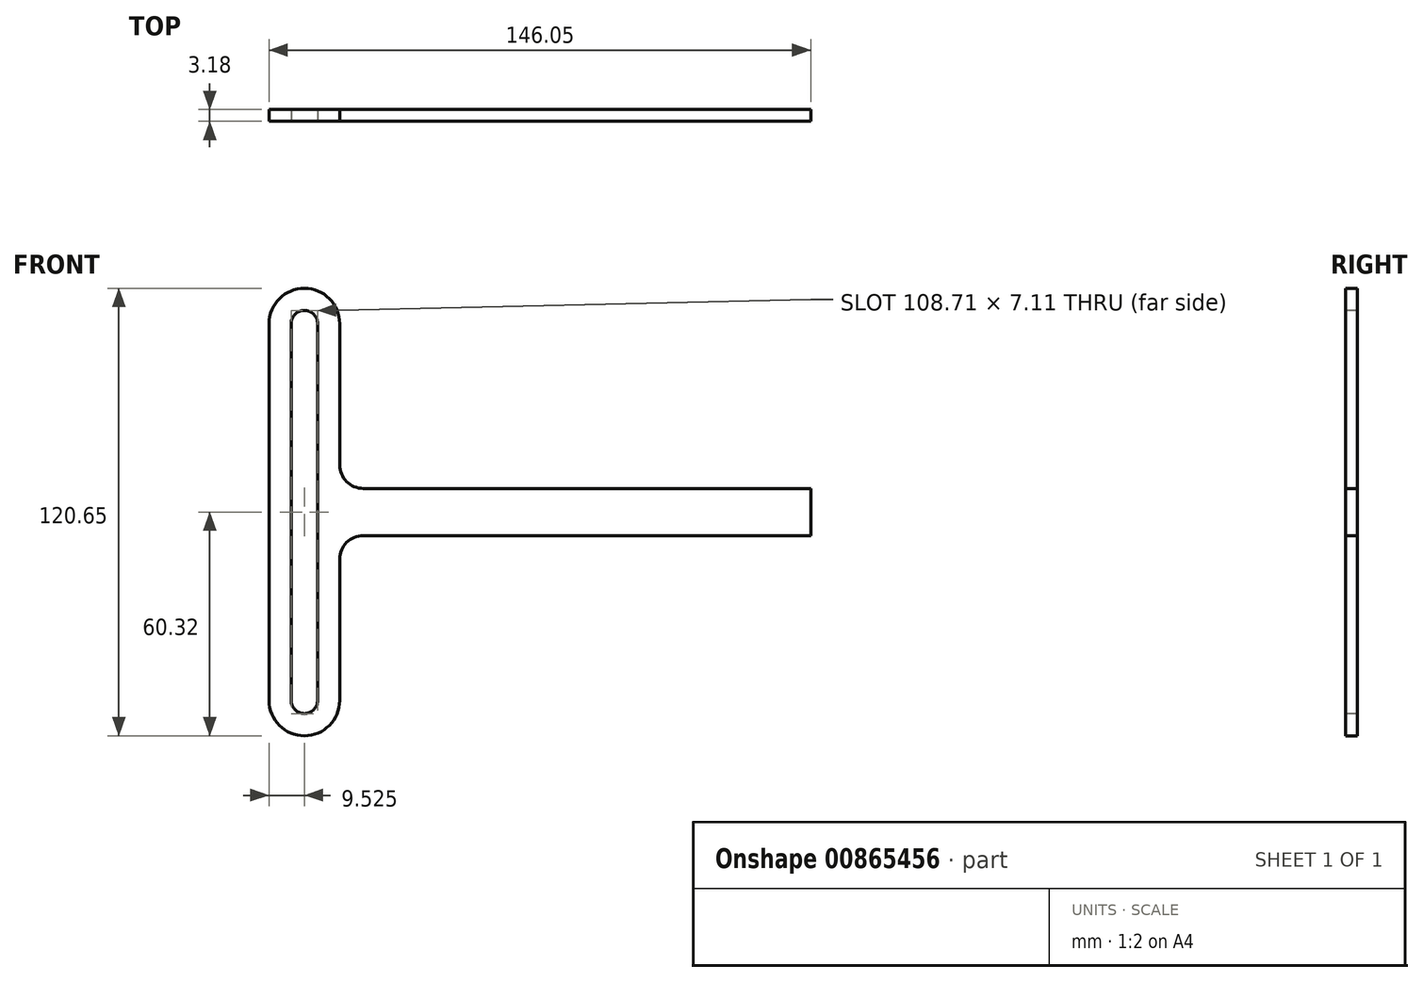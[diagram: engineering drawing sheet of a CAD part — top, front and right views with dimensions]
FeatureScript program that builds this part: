
annotation { "Feature Type Name" : "Feature", "Feature Type Description" : "" }
export const myFeature = defineFeature(function(context is Context, id is Id, definition is map)
    precondition{}
    {
        {
            var Q0;
            Q0=qCreatedBy(makeId("Front.planeOp"),FACE);
            var sketch = newSketch(context, id + "F0", { "sketchPlane" : qUnion([Q0])});
            skLineSegment(sketch, "E0.bottom", {"start": v(6.35, 0) * mm, "end": v(127, 0) * mm});
            skLineSegment(sketch, "E0.top", {"start": v(6.35, -12.7) * mm, "end": v(127, -12.7) * mm});
            skLineSegment(sketch, "E0.right", {"start": v(127, 0) * mm, "end": v(127, -12.7) * mm});
            skLineSegment(sketch, "E1", {"start": v(0, 6.35) * mm, "end": v(0, 44.45) * mm});
            skLineSegment(sketch, "E2", {"start": v(-19.05, 44.45) * mm, "end": v(-19.05, -57.15) * mm});
            skLineSegment(sketch, "E3", {"start": v(0, -57.15) * mm, "end": v(0, -19.05) * mm});
            skArc(sketch, "E4", {"start": v(0, 44.45) * mm, "mid": v(-9.52, 53.98) * mm, "end": v(-19.05, 44.45) * mm});
            skArc(sketch, "E5", {"start": v(-19.05, -57.15) * mm, "mid": v(-9.52, -66.68) * mm, "end": v(0, -57.15) * mm});
            skPoint(sketch, "E6.visualSharp", {"position": v(0, 0) * mm});
            skArc(sketch, "E6.filletArc", {"start": v(0, 6.35) * mm, "mid": v(1.86, 1.86) * mm, "end": v(6.35, 0) * mm});
            skPoint(sketch, "E7.visualSharp", {"position": v(0, -12.7) * mm});
            skArc(sketch, "E7.filletArc", {"start": v(6.35, -12.7) * mm, "mid": v(1.86, -14.56) * mm, "end": v(0, -19.05) * mm});
            skSolve(sketch);
        }
        {
            var Q0;
            Q0=qSketchRegion(id+"F0",true);
            extrude(context, id + "F1", {"entities" : qUnion([Q0]), "depth" : 3.17 * mm, "offsetDistance" : 25.4 * mm});
        }
        {
            var Q0;
            Q0=makeQuery(id+"F1.opExtrude","CAP_FACE",FACE,{"disambiguationData":[OSD([sQuery(id+"F0.wireOp",EDGE,"E0.bottom"),sQuery(id+"F0.wireOp",EDGE,"E0.top"),sQuery(id+"F0.wireOp",EDGE,"E0.right"),sQuery(id+"F0.wireOp",EDGE,"E1"),sQuery(id+"F0.wireOp",EDGE,"E2"),sQuery(id+"F0.wireOp",EDGE,"E3"),sQuery(id+"F0.wireOp",EDGE,"E4"),sQuery(id+"F0.wireOp",EDGE,"E5"),sQuery(id+"F0.wireOp",EDGE,"E6.filletArc"),sQuery(id+"F0.wireOp",EDGE,"E7.filletArc")])],"isStart":false});
            var sketch = newSketch(context, id + "F2", { "sketchPlane" : qUnion([Q0])});
            skArc(sketch, "E8.0", {"start": v(-5.97, 44.45) * mm, "mid": v(-9.52, 48) * mm, "end": v(-13.08, 44.45) * mm});
            skLineSegment(sketch, "E8.1", {"start": v(-5.97, 6.35) * mm, "end": v(-5.97, 44.45) * mm});
            skLineSegment(sketch, "E8.2", {"start": v(-13.08, 44.45) * mm, "end": v(-13.08, -57.15) * mm});
            skArc(sketch, "E8.6", {"start": v(-13.08, -57.15) * mm, "mid": v(-9.52, -60.7) * mm, "end": v(-5.97, -57.15) * mm});
            skLineSegment(sketch, "E8.7", {"start": v(-5.97, -57.15) * mm, "end": v(-5.97, -19.05) * mm});
            skLineSegment(sketch, "E9", {"start": v(-5.97, 6.35) * mm, "end": v(-5.97, -19.05) * mm});
            skSolve(sketch);
        }
        {
            var Q0;
            Q0=qSketchRegion(id+"F2",true);
            extrude(context, id + "F3", {"entities" : qUnion([Q0]), "operationType" : NewBodyOperationType.REMOVE, "oppositeDirection" : true, "depth" : 25.4 * mm, "offsetDistance" : 25.4 * mm});
        }
    });
